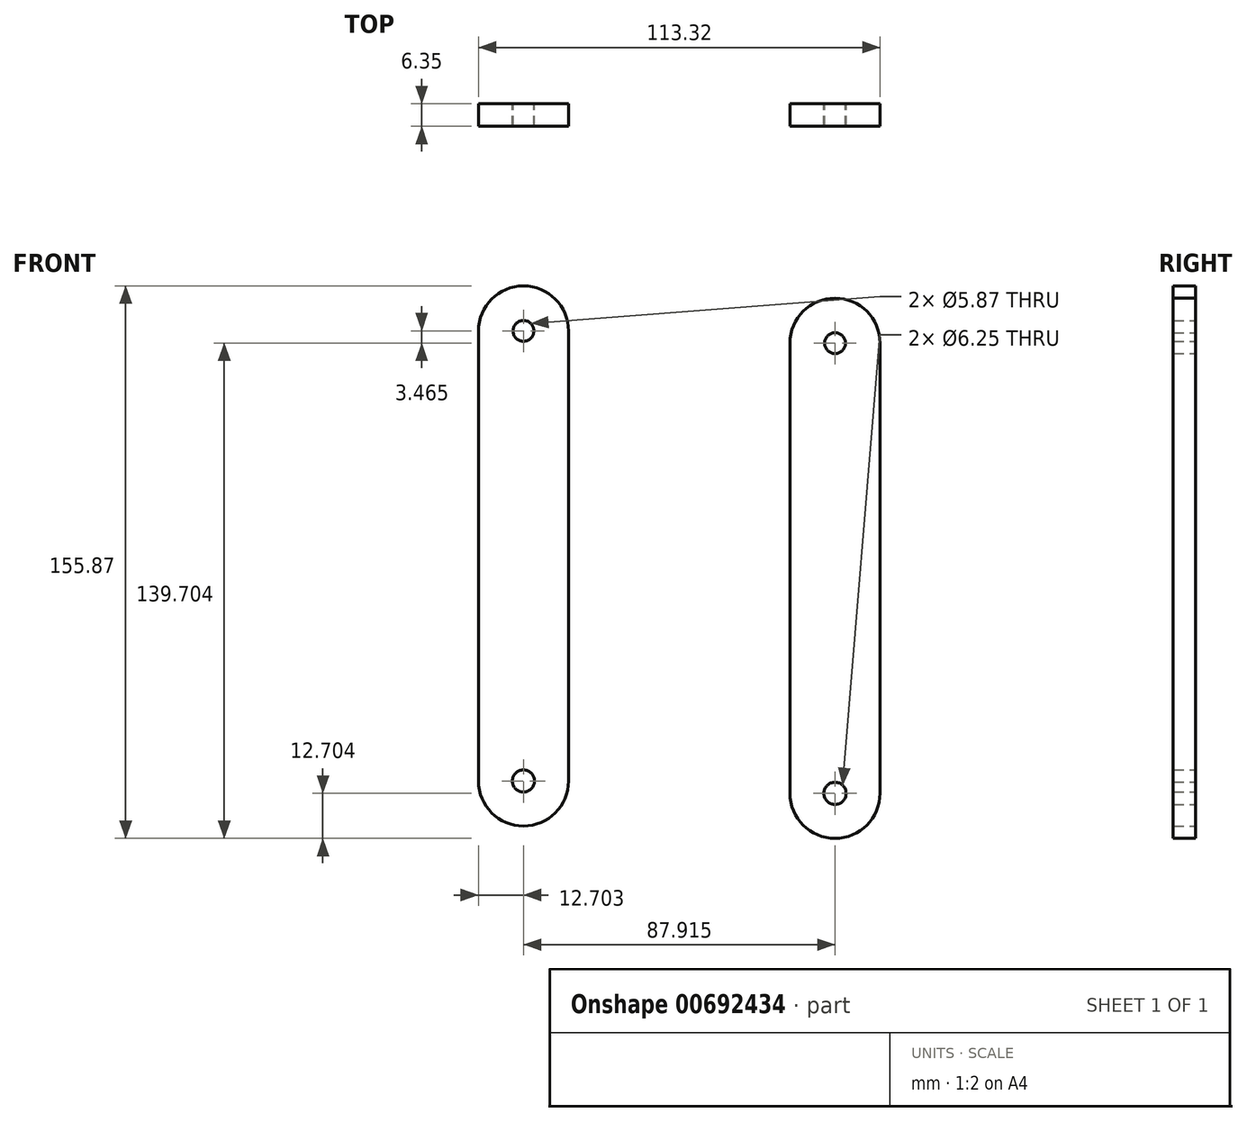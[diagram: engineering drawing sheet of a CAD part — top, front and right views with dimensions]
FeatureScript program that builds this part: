
annotation { "Feature Type Name" : "Feature", "Feature Type Description" : "" }
export const myFeature = defineFeature(function(context is Context, id is Id, definition is map)
    precondition{}
    {
        {
            var Q0;
            Q0=qCreatedBy(makeId("Front.planeOp"),FACE);
            var sketch = newSketch(context, id + "F0", { "sketchPlane" : qUnion([Q0])});
            skLineSegment(sketch, "E0", {"start": v(-75.26, 64.09) * mm, "end": v(-75.26, -62.91) * mm});
            skLineSegment(sketch, "E1", {"start": v(-49.86, 64.09) * mm, "end": v(-49.86, -62.91) * mm});
            skArc(sketch, "E2", {"start": v(-75.26, 64.09) * mm, "mid": v(-62.56, 76.79) * mm, "end": v(-49.86, 64.09) * mm});
            skArc(sketch, "E3", {"start": v(-75.26, -62.91) * mm, "mid": v(-62.56, -75.61) * mm, "end": v(-49.86, -62.91) * mm});
            skCircle(sketch, "E4", {"center": v(-62.56, 64.09) * mm, "radius": 2.94 * mm});
            skCircle(sketch, "E5", {"center": v(-62.56, -62.91) * mm, "radius": 3.13 * mm});
            skLineSegment(sketch, "E6", {"start": v(12.66, 60.62) * mm, "end": v(12.66, -66.38) * mm});
            skLineSegment(sketch, "E7", {"start": v(38.06, 60.62) * mm, "end": v(38.06, -66.38) * mm});
            skArc(sketch, "E8", {"start": v(12.66, 60.62) * mm, "mid": v(25.36, 73.32) * mm, "end": v(38.06, 60.62) * mm});
            skArc(sketch, "E9", {"start": v(12.66, -66.38) * mm, "mid": v(25.36, -79.08) * mm, "end": v(38.06, -66.38) * mm});
            skCircle(sketch, "E10", {"center": v(25.36, 60.62) * mm, "radius": 2.94 * mm});
            skCircle(sketch, "E11", {"center": v(25.36, -66.38) * mm, "radius": 3.13 * mm});
            skSolve(sketch);
        }
        {
            var Q0;
            Q0=makeQuery(id+"F0.imprint","IMPRINT",FACE,{"disambiguationData":[TD([[makeQuery(id+"F0.imprint","IMPRINT",EDGE,{"derivedFrom":sQuery(id+"F0.wireOp",EDGE,"E6")}),1.0]])]});
            var Q1;
            Q1=makeQuery(id+"F0.imprint","IMPRINT",FACE,{"disambiguationData":[TD([[makeQuery(id+"F0.imprint","IMPRINT",EDGE,{"derivedFrom":sQuery(id+"F0.wireOp",EDGE,"E0")}),1.0]])]});
            extrude(context, id + "F1", {"entities" : qUnion([Q0, Q1]), "depth" : 6.35 * mm, "offsetDistance" : 25.4 * mm});
        }
    });
